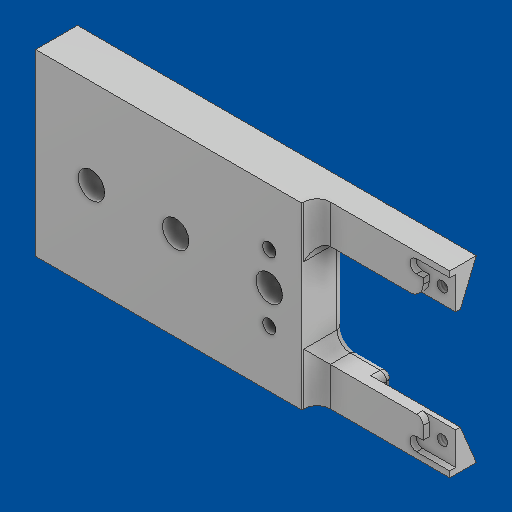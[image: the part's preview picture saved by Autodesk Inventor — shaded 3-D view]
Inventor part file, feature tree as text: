
AUTODESK INVENTOR PART (.ipt)
format: ipt  version: 2025 (Build 290162000, 162)  size: 222,208 bytes
history: native  units: in
note: dims shown in document units (in); Inventor stores cm internally (conversion verified against a paired STEP export)
features: fillet x3, direct_edit x3, other x3, move_body x2, hole x1, sketch x1
ambient origin geometry x8: Origin, YZ Plane, XZ Plane, XY Plane, X Axis, Y Axis, Z Axis, Center Point
bodies: Solid1 (feature_tree), Body1 (feature_tree)
feature tree (13):
  fillet  "Fillet1"  Radius=0.0394in
  direct_edit  "Direct Edit1"
  fillet  "Fillet2"  [1 undecoded]
  fillet  "Fillet3"  Radius=0.0394in
  direct_edit  "Direct Edit2"
  direct_edit  "Direct Edit3"
  hole  "Hole1"  [1 undecoded]
  sketch  "Sketch1"  dims[d1=0.0in d2=0.0in d3=-0.002in d4=0.0in d5=0.0in d6=-0.002in d7=0.0394in d8=0.0787in d9=-0.0079in d10=-0.0079in d11=0.0315in d12=0.0118in d13=0.0118in d14=0.0617in d15=0.1575in d16=0.1575in d17=0.0787in d18=90.0deg d19=0.248in d20=0.8108in]
  move_body  "Move1"
  move_body  "Move2"
  other  "Size1"
  other  "Size2"
  other  "Size3"
note: 2 required parameter values undecoded (feature->parameter linkage not recoverable at this tier; creation-order binding heuristic only, values carry confidence <= 0.55)
